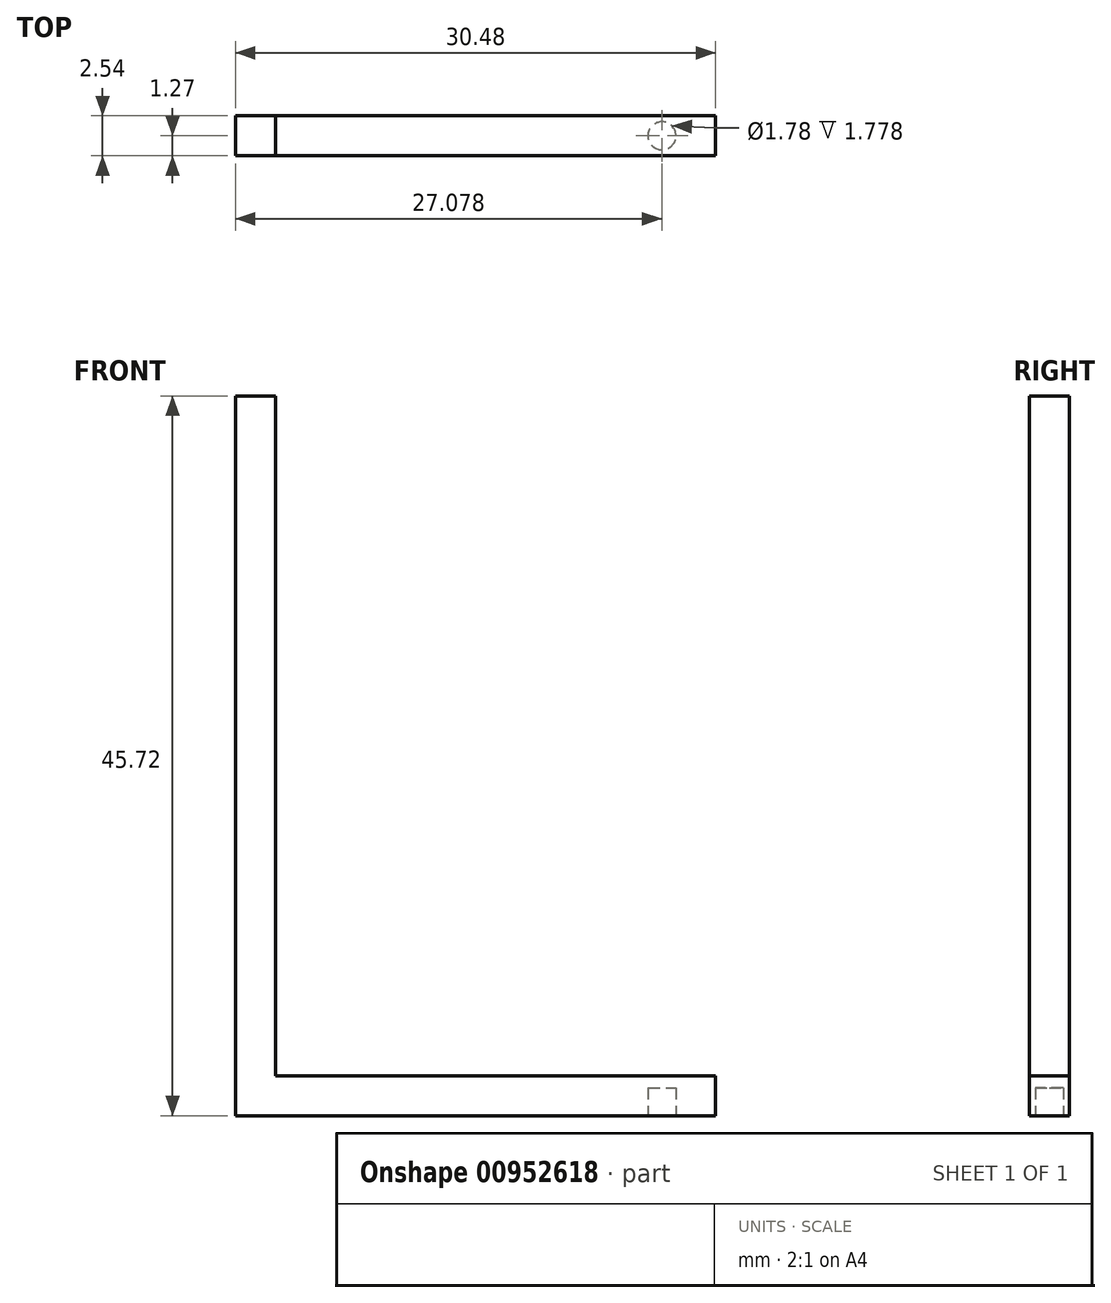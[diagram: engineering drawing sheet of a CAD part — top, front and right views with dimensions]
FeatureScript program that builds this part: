
annotation { "Feature Type Name" : "Feature", "Feature Type Description" : "" }
export const myFeature = defineFeature(function(context is Context, id is Id, definition is map)
    precondition{}
    {
        {
            var Q0;
            Q0=qCreatedBy(makeId("Front.planeOp"),FACE);
            var sketch = newSketch(context, id + "F0", { "sketchPlane" : qUnion([Q0])});
            skLineSegment(sketch, "E0.bottom", {"start": v(0, 0) * mm, "end": v(2.54, 0) * mm});
            skLineSegment(sketch, "E0.top", {"start": v(0, 45.72) * mm, "end": v(2.54, 45.72) * mm});
            skLineSegment(sketch, "E0.left", {"start": v(0, 0) * mm, "end": v(0, 45.72) * mm});
            skLineSegment(sketch, "E0.right", {"start": v(2.54, 0) * mm, "end": v(2.54, 45.72) * mm});
            skLineSegment(sketch, "E1.bottom", {"start": v(0, 0) * mm, "end": v(30.48, 0) * mm});
            skLineSegment(sketch, "E1.top", {"start": v(0, 2.54) * mm, "end": v(30.48, 2.54) * mm});
            skLineSegment(sketch, "E1.left", {"start": v(0, 0) * mm, "end": v(0, 2.54) * mm});
            skLineSegment(sketch, "E1.right", {"start": v(30.48, 0) * mm, "end": v(30.48, 2.54) * mm});
            skSolve(sketch);
        }
        {
            var Q0;
            Q0 = qSketchRegion(id + "F0", true);
            extrude(context, id + "F1", {"entities" : qUnion([Q0]), "depth" : 2.54 * mm, "offsetDistance" : 25.4 * mm});
        }
        {
            var Q0;
            Q0=makeQuery(id+"F1.opExtrude","SWEPT_FACE",FACE,{"disambiguationData":[OSD([sQuery(id+"F0.wireOp",EDGE,"E1.bottom")])]});
            var sketch = newSketch(context, id + "F2", { "sketchPlane" : qUnion([Q0])});
            skLineSegment(sketch, "E2", {"start": v(30.48, 1.27) * mm, "end": v(0, 1.27) * mm});
            skCircle(sketch, "E3", {"center": v(27.08, 1.27) * mm, "radius": 0.89 * mm});
            skSolve(sketch);
        }
        {
            var Q0;
            Q0 = qSketchRegion(id + "F2", true);
            extrude(context, id + "F3", {"entities" : qUnion([Q0]), "operationType" : NewBodyOperationType.REMOVE, "oppositeDirection" : true, "depth" : 1.78 * mm, "offsetDistance" : 25.4 * mm});
        }
    });
